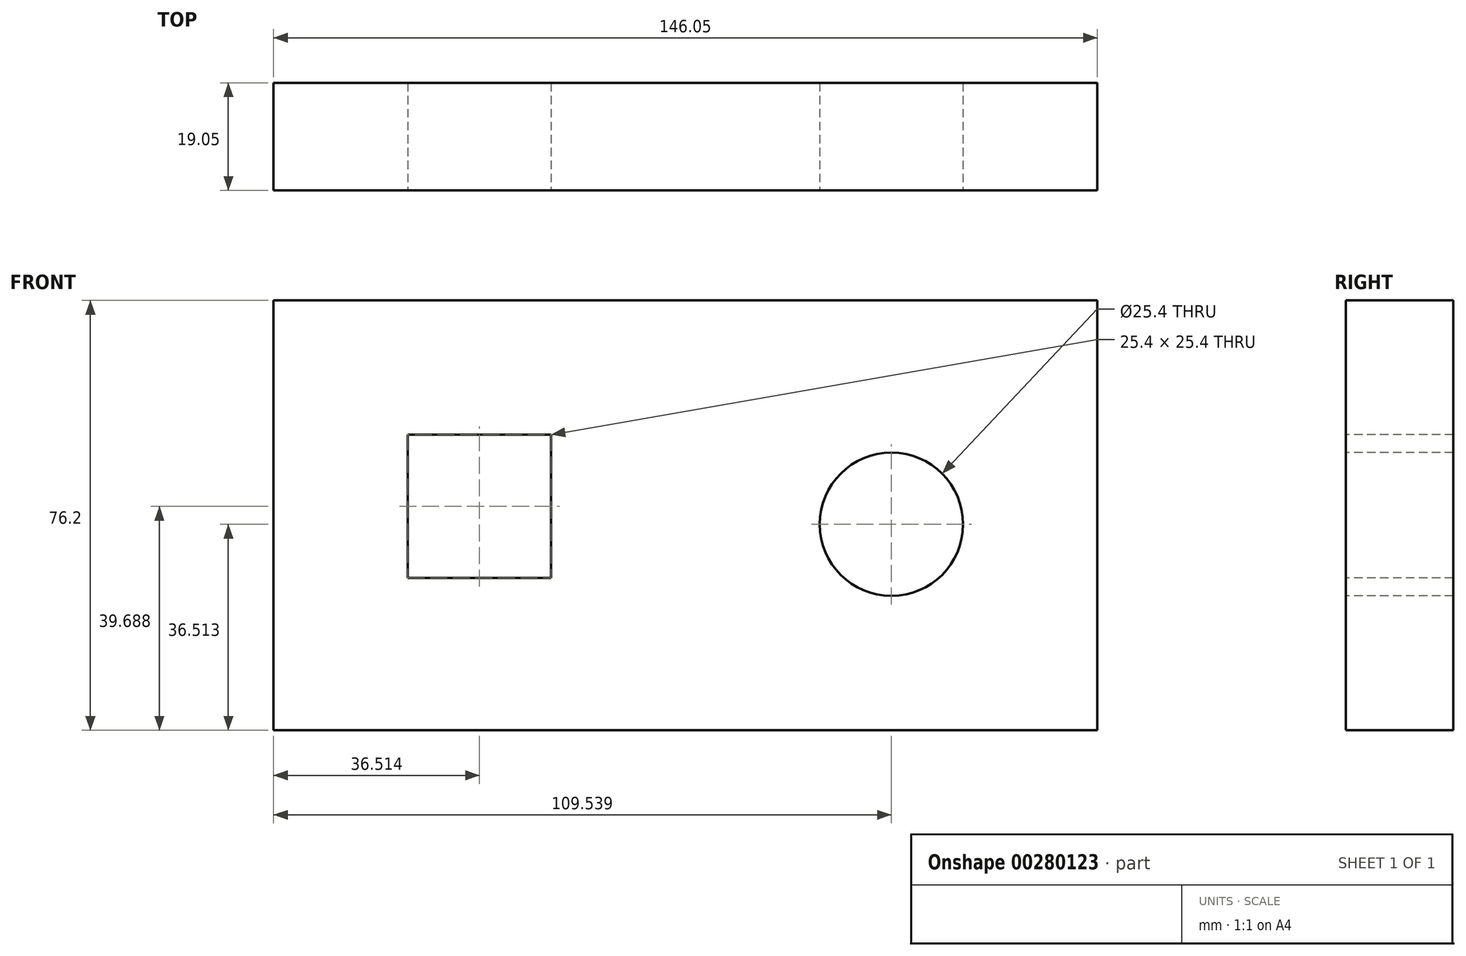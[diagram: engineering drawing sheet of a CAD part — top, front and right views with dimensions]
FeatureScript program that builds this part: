
annotation { "Feature Type Name" : "Feature", "Feature Type Description" : "" }
export const myFeature = defineFeature(function(context is Context, id is Id, definition is map)
    precondition{}
    {
        {
            var Q0;
            Q0=qCreatedBy(makeId("Front.planeOp"),FACE);
            var sketch = newSketch(context, id + "F0", { "sketchPlane" : qUnion([Q0])});
            skLineSegment(sketch, "E0.bottom", {"start": v(-103.28, 61.73) * mm, "end": v(42.77, 61.73) * mm});
            skLineSegment(sketch, "E0.top", {"start": v(-103.28, -14.47) * mm, "end": v(42.77, -14.47) * mm});
            skLineSegment(sketch, "E0.left", {"start": v(-103.28, 61.73) * mm, "end": v(-103.28, -14.47) * mm});
            skLineSegment(sketch, "E0.right", {"start": v(42.77, 61.73) * mm, "end": v(42.77, -14.47) * mm});
            skSolve(sketch);
        }
        {
            var Q0;
            Q0 = qSketchRegion(id + "F0", true);
            extrude(context, id + "F1", {"entities" : qUnion([Q0]), "depth" : 19.05 * mm});
        }
        {
            var Q0;
            Q0=makeQuery(id+"F1.opExtrude","CAP_FACE",FACE,{"disambiguationData":[OSD([sQuery(id+"F0.wireOp",EDGE,"E0.bottom"),sQuery(id+"F0.wireOp",EDGE,"E0.top"),sQuery(id+"F0.wireOp",EDGE,"E0.left"),sQuery(id+"F0.wireOp",EDGE,"E0.right")])],"isStart":false});
            var sketch = newSketch(context, id + "F2", { "sketchPlane" : qUnion([Q0])});
            skCircle(sketch, "E1", {"center": v(6.26, 22.04) * mm, "radius": 12.7 * mm});
            skSolve(sketch);
        }
        {
            var Q0;
            Q0 = qSketchRegion(id + "F2", true);
            extrude(context, id + "F3", {"entities" : qUnion([Q0]), "operationType" : NewBodyOperationType.REMOVE, "oppositeDirection" : true, "depth" : 19.05 * mm});
        }
        {
            var Q0;
            Q0=makeQuery(id+"F1.opExtrude","CAP_FACE",FACE,{"disambiguationData":[OSD([sQuery(id+"F0.wireOp",EDGE,"E0.bottom"),sQuery(id+"F0.wireOp",EDGE,"E0.top"),sQuery(id+"F0.wireOp",EDGE,"E0.left"),sQuery(id+"F0.wireOp",EDGE,"E0.right")])],"isStart":false});
            var sketch = newSketch(context, id + "F4", { "sketchPlane" : qUnion([Q0])});
            skLineSegment(sketch, "E2.bottom", {"start": v(-79.47, 37.92) * mm, "end": v(-54.07, 37.92) * mm});
            skLineSegment(sketch, "E2.top", {"start": v(-79.47, 12.52) * mm, "end": v(-54.07, 12.52) * mm});
            skLineSegment(sketch, "E2.left", {"start": v(-79.47, 37.92) * mm, "end": v(-79.47, 12.52) * mm});
            skLineSegment(sketch, "E2.right", {"start": v(-54.07, 37.92) * mm, "end": v(-54.07, 12.52) * mm});
            skSolve(sketch);
        }
        {
            var Q0;
            Q0 = qSketchRegion(id + "F4", true);
            extrude(context, id + "F5", {"entities" : qUnion([Q0]), "operationType" : NewBodyOperationType.REMOVE, "oppositeDirection" : true, "depth" : 19.05 * mm});
        }
    });
